# Revit family: Floor_Standing_Bottle_Filling_Station-Elkay-DSSBF8SP
name_source: partatom
category: Plumbing Fixtures
units: mm (PartAtom-declared; Revit-internal decimal feet)

## family parameters
Always vertical = Yes
Cut with Voids When Loaded = No
Maintain Annotation Orientation = No
OmniClass Number = 23.65.70.14.11
OmniClass Title = Drinking Fountains/Coolers
Part Type = Normal
Room Calculation Point = No
Round Connector Dimension = Use Diameter
Shared = No
Work Plane-Based = No

## types (1)
- DSSBF8SP (Floor Standing Bottle Filling Station)
    Activation Method = Electronic Bottle Filler Sensor
    Approx. Shipping Weight (lbs) = 94
    Assembly Code = D2010800
    CWFU = 0
    Chilling Capacity (GPH) = 8
    Current = 0 A
    Default Elevation = 0 "
    Description = Enhanced ezH2O® Floor Standing Bottle Filling Station Filtered Refrigerated Stainless Steel
    HWFU = 0
    Height = 48 "
    Inlet Connection Size (inch) = 0.375 "
    Length = 21.5 "
    Main Material = Finish-Elkay-Steel
    Manufacturer = Elkay Manufacturer Company
    Manufacturer Brand = Elkay (by Zurn Elkay Water Solutions)
    Model = DSSBF8SP
    Number of Poles = 1
    Outlet Connection Size (inch) = 1.5 "
    Power Factor = 1
    Product Documentation Link = https://www.elkayfiles.com
    Product Installation Sheet URL = https://www.elkayfiles.com
    Product Page URL = https://www.elkay.com
    Product Weight (lbs) = 84
    Product data URL = https://bimobject.com
    Repair Parts URL = https://www.elkayfiles.com
    URL = https://www.elkay.com
    Voltage = 115 V
    WFU = 0
    Water Outlet = 26.125 "
    Water Supply = 23.063 "
    Width = 15 "

## geometry (parser evidence)
native form markers: Sweep x5
no freeform markers — native parametric forms only
